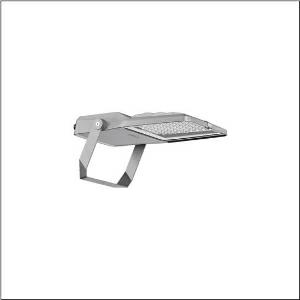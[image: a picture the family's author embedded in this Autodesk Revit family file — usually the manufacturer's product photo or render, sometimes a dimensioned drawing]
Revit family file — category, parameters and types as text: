
# Revit family: floodlight_fl_21_mini___pl52_5xa7773c4d1a_b58d
name_source: partatom
category: Lighting Fixtures
units: mm (PartAtom-declared; Revit-internal decimal feet)

## family parameters
Cut with Voids When Loaded = No
Host = Face
Light Source = No
Part Type = Normal
Room Calculation Point = No
Round Connector Dimension = Use Diameter
Shared = No

## types (1)
- --- (1 x LED, 20360 lm, 163.5 W, 4000K)
    Apparent Load = 163 VA
    CIE Flux Codes = 26 60 98 100 100
    Color Rendering = 70
    Color Temperature = 4000K
    Default Elevation = 1800 mm
    Description = Floodlight FL 21 mini, floodlight, primary light control with lens, of PMMA, primary optical cover: protective disc, of toughened safety glass, transparent, light distribution: PL52, light emission: direct distribution, installation type: surface-mounted, LED, High Power LED, rated luminous flux: 20.360lm, luminous efficacy: 125lm/W, light colour: 740, colour temperature: 4000K, control gear: ON/OFF Multilumen, control: pre-setting: linear dimming characteristic, Temp-Guard, with terminal, 6-pole, mains connection: 220..240V, AC, 50/60Hz, start of lifetime: 164W, luminaire housing, of diecast aluminium, powder-coated, SITECO metallic grey (DB 702S), corrosivity category C5 mid according to DIN EN ISO 12944, suitable for swimming pools, chlorine-resistant, sealing non-destructively replaceable, mounting bracket, of steel, galvanised, powder-coated, SITECO metallic grey (DB 702S), ON/OFF, protection rating (complete): IP66, insulation class (complete): insulation class I (protective earthing), certification: CE, ENEC, VDE, protection symbol: D, impact resistance: IK08, permissible operating ambient temperature: -40..+40°C, permissible operating ambient temperature for outdoor applications: -40..+50°C, standard: DIN EN 12944, LABS conformity tested according to VDMA 24364:2018-05, packaging unit: 1 piece

Light Distribution: PL52
    Height = 70 mm
    Lamp = 1 x LED
    Lamp Light Flux = 20360 lm
    Lamp Power = 163.5 W
    Lamp count = 1
    Length = 485 mm
    Luminous efficacy = 125 lm/W
    Manufacturer = Siteco
    ModVariant = No
    Model = 5XA7773C4D1A
    Number of Poles = 1
    OnlyDefault = Yes
    Power Factor = 1
    Product Name = Floodlight FL 21 mini | PL52
    Product group = floodlight | pylon annexe
    ProductGroupID = 6201
    Protection Class = Protection class I
    Protection Degree = IP 66
    RLX_Detail_Level = 1
    RLX_Emergency_Light_Flux = 0 lm
    RLX_Emergency_Type = 0
    RLX_Emergency_Type_DB = No
    RlxData = <blob elided: 94401 chars, md5=ecbfff52>
    Socket = socket
    Standby Power = 0 W
    System Light Flux = 20360 lm
    System Power = 163 W
    Type Comments = factory setting: luminous flux: 100 % | (ON | - | - | - | - | - | - | -) | 825 mA
    Type Image = l_1006845.jpg
    URL = http://relux.com
    VarID = @adj_163561
    Voltage = 0 V
    Weight = 0.00 kg
    Width = 337 mm

## geometry (parser evidence)
native form markers: Blend x4, Sweep x14
no freeform markers — native parametric forms only
